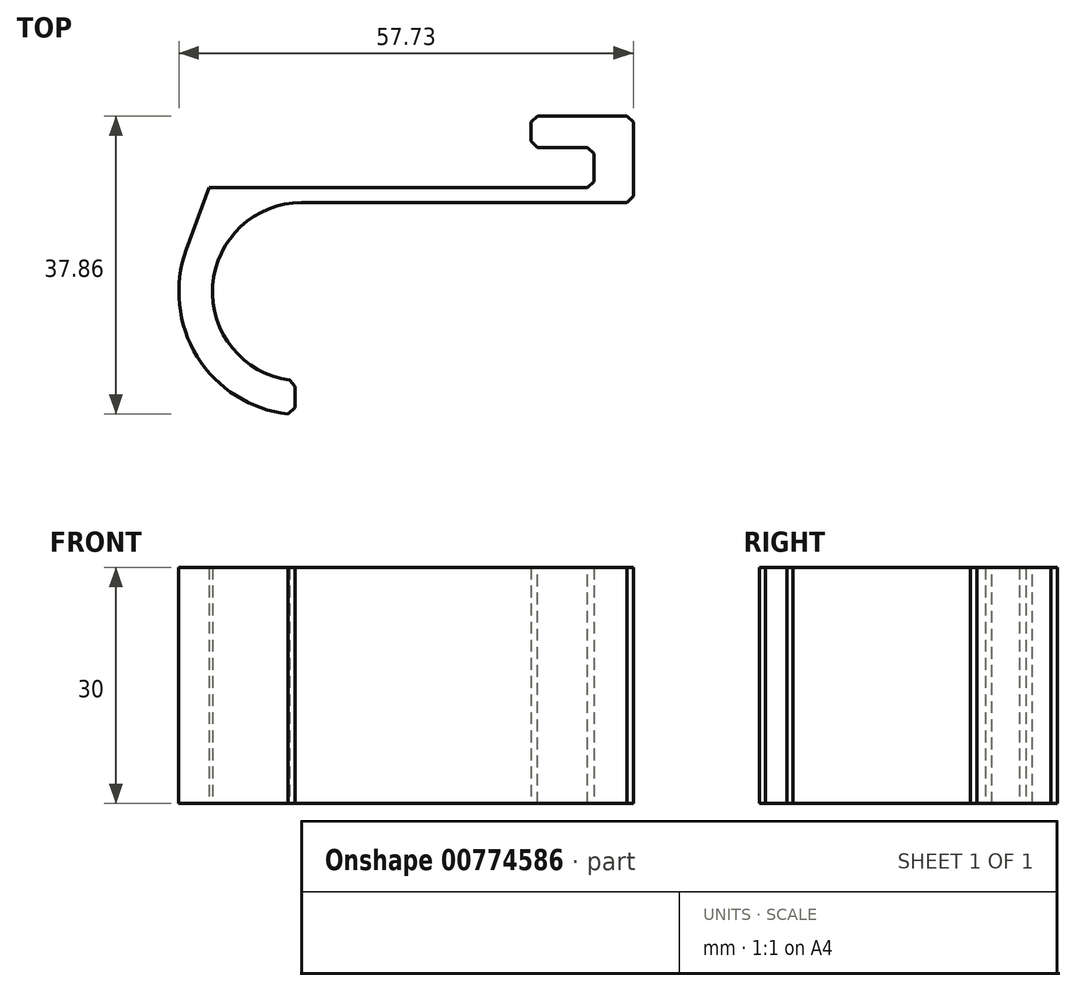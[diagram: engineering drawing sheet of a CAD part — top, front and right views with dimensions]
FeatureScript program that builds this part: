
annotation { "Feature Type Name" : "Feature", "Feature Type Description" : "" }
export const myFeature = defineFeature(function(context is Context, id is Id, definition is map)
    precondition{}
    {
        {
            var Q0;
            Q0=qCreatedBy(makeId("Top.planeOp"),FACE);
            var sketch = newSketch(context, id + "F0", { "sketchPlane" : qUnion([Q0])});
            skLineSegment(sketch, "E0.bottom", {"start": v(0, 0) * mm, "end": v(8, 0) * mm});
            skLineSegment(sketch, "E0.top", {"start": v(0, 4) * mm, "end": v(13, 4) * mm});
            skLineSegment(sketch, "E0.left", {"start": v(0, 0) * mm, "end": v(0, 4) * mm});
            skLineSegment(sketch, "E1.right", {"start": v(8, 0) * mm, "end": v(8, -5.11) * mm});
            skLineSegment(sketch, "E2.top", {"start": v(8, -5.11) * mm, "end": v(0, -5.11) * mm});
            skPoint(sketch, "E3", {"position": v(0, -7.01) * mm});
            skLineSegment(sketch, "E4.0", {"start": v(-40.92, -5.11) * mm, "end": v(-40.92, -5.11) * mm});
            skPoint(sketch, "E5", {"position": v(0, -32.83) * mm});
            skPoint(sketch, "E6.start.orphan", {"position": v(0, -28.83) * mm});
            skArc(sketch, "E7.0", {"start": v(-29.13, -7.01) * mm, "mid": v(-37.1, -10.3) * mm, "end": v(-40.46, -18.23) * mm});
            skLineSegment(sketch, "E8", {"start": v(0, -7.01) * mm, "end": v(13, -7.01) * mm});
            skArc(sketch, "E9.trimOffspring", {"start": v(-43.8, -13.01) * mm, "mid": v(-44.49, -15.58) * mm, "end": v(-44.73, -18.23) * mm});
            skLineSegment(sketch, "E10", {"start": v(0, -7.01) * mm, "end": v(-29.13, -7.01) * mm});
            skLineSegment(sketch, "E11", {"start": v(-40.92, -5.11) * mm, "end": v(-43.8, -13.01) * mm});
            skPoint(sketch, "E12", {"position": v(0, -5.11) * mm});
            skLineSegment(sketch, "E13", {"start": v(13, 4) * mm, "end": v(13, -7.01) * mm});
            skLineSegment(sketch, "E14", {"start": v(-40.92, -5.11) * mm, "end": v(-30, -5.11) * mm});
            skArc(sketch, "E15", {"start": v(-40.46, -18.23) * mm, "mid": v(-37.49, -26) * mm, "end": v(-30, -29.65) * mm});
            skArc(sketch, "E16", {"start": v(-44.73, -18.23) * mm, "mid": v(-40.5, -29.03) * mm, "end": v(-30, -33.93) * mm});
            skLineSegment(sketch, "E17", {"start": v(-44.73, -18.23) * mm, "end": v(-40.46, -18.23) * mm, "construction": true});
            skLineSegment(sketch, "E18", {"start": v(8, -5.11) * mm, "end": v(8, -7.01) * mm, "construction": true});
            skLineSegment(sketch, "E19", {"start": v(8, -5.11) * mm, "end": v(13, -5.11) * mm, "construction": true});
            skLineSegment(sketch, "E20", {"start": v(-30, -33.93) * mm, "end": v(-30, -29.65) * mm});
            skLineSegment(sketch, "E21", {"start": v(-30, -29.65) * mm, "end": v(-30, -7.05) * mm, "construction": true});
            skLineSegment(sketch, "E22", {"start": v(-30, -7.05) * mm, "end": v(-30, -5.11) * mm, "construction": true});
            skLineSegment(sketch, "E23", {"start": v(-30, -5.11) * mm, "end": v(0, -5.11) * mm});
            skSolve(sketch);
        }
        {
            var Q0;
            Q0=makeQuery(id+"F0.imprint","IMPRINT",FACE,{"disambiguationData":[TD([[makeQuery(id+"F0.imprint","IMPRINT",EDGE,{"derivedFrom":sQuery(id+"F0.wireOp",EDGE,"E0.bottom")}),1.0]])]});
            extrude(context, id + "F1", {"entities" : qUnion([Q0]), "depth" : 30 * mm, "offsetDistance" : 25 * mm});
        }
        {
            var Q0;
            Q0=makeQuery(id+"F1.opExtrude","SWEPT_EDGE",EDGE,{"disambiguationData":[OSD([sQuery(id+"F0.wireOp",EDGE,"E0.bottom"),sQuery(id+"F0.wireOp",EDGE,"E0.left")])]});
            var Q1;
            Q1=makeQuery(id+"F1.opExtrude","SWEPT_EDGE",EDGE,{"disambiguationData":[OSD([sQuery(id+"F0.wireOp",EDGE,"E0.top"),sQuery(id+"F0.wireOp",EDGE,"E0.left")])]});
            var Q2;
            Q2=makeQuery(id+"F1.opExtrude","SWEPT_EDGE",EDGE,{"disambiguationData":[OSD([sQuery(id+"F0.wireOp",EDGE,"E0.bottom"),sQuery(id+"F0.wireOp",EDGE,"E1.right")])]});
            var Q3;
            Q3=makeQuery(id+"F1.opExtrude","SWEPT_EDGE",EDGE,{"disambiguationData":[OSD([sQuery(id+"F0.wireOp",EDGE,"E1.right"),sQuery(id+"F0.wireOp",EDGE,"E2.top")])]});
            var Q4;
            Q4=makeQuery(id+"F1.opExtrude","SWEPT_EDGE",EDGE,{"disambiguationData":[OSD([sQuery(id+"F0.wireOp",EDGE,"E8"),sQuery(id+"F0.wireOp",EDGE,"E13")])]});
            var Q5;
            Q5=makeQuery(id+"F1.opExtrude","SWEPT_EDGE",EDGE,{"disambiguationData":[OSD([sQuery(id+"F0.wireOp",EDGE,"E0.top"),sQuery(id+"F0.wireOp",EDGE,"E13")])]});
            var Q6;
            Q6=makeQuery(id+"F1.opExtrude","SWEPT_EDGE",EDGE,{"disambiguationData":[OSD([sQuery(id+"F0.wireOp",EDGE,"E16"),sQuery(id+"F0.wireOp",EDGE,"E20")])]});
            var Q7;
            Q7=makeQuery(id+"F1.opExtrude","SWEPT_EDGE",EDGE,{"disambiguationData":[OSD([sQuery(id+"F0.wireOp",EDGE,"E15"),sQuery(id+"F0.wireOp",EDGE,"E20")])]});
            chamfer(context, id + "F2", {"entities" : qUnion([Q0, Q1, Q2, Q3, Q4, Q5, Q6, Q7]), "width" : 0.8 * mm, "tangentPropagation" : true});
        }
    });
